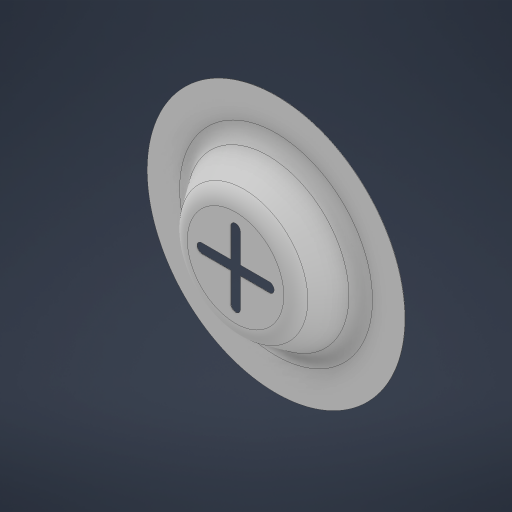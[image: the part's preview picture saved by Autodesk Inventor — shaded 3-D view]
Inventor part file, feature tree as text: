
AUTODESK INVENTOR PART (.ipt)
format: ipt  version: 2024.3 (Build 283343010, 343A)  size: 258,048 bytes
history: native  units: mm
features: sketch x2, revolve x1, extrude x1
ambient origin geometry x8: Origin, YZ Plane, XZ Plane, XY Plane, X Axis, Y Axis, Z Axis, Center Point
bodies: Volumenkörper1 (feature_tree)
feature tree (4):
  revolve  "Umdrehung1"
  extrude  "Extrusion1"  Depth=10.0mm
  sketch  "Skizze1"  dims[d0=0.02mm d2=10.0mm]
  sketch  "Skizze2"  dims[d3=0.02mm d4=1.0mm d5=2.1mm d6=5.0mm d7=90.0deg d8=4.0mm d9=0.5mm d10=40.0mm d12=360.0deg d14=0.0mm d15=0.0mm]
